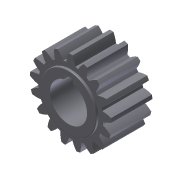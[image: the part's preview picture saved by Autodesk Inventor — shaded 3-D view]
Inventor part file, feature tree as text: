
AUTODESK INVENTOR PART (.ipt)
format: ipt  version: 2011 (Build 150239000, 239)  size: 233,472 bytes
history: native  units: mm (DEFAULTED — no unit token found)
features: other x4, sketch x4, extrude x3, plane x3, fillet x1
ambient origin geometry x8: Origin, YZ Plane, XZ Plane, XY Plane, X Axis, Y Axis, Z Axis, Center Point
bodies: Solid1 (feature_tree)
feature tree (15):
  other  "Gear 17T 20dp 500key"
  extrude  "Extrusion1"  Depth=13.97mm TaperAngle=0.0deg
  plane  "Work Plane1"
  plane  "Work Plane2"
  plane  "Work Plane3"
  other  "Spur Gear"
  extrude  "Extrusion2"  Depth=76.2mm TaperAngle=0.0deg
  extrude  "Extrusion3"  TaperAngle=0.0deg  [1 undecoded]
  fillet  "Fillet1"  Radius=63.5mm
  sketch  "Sketch1"  dims[d0=27.94mm d1=13.97mm d2=0.0mm]
  sketch  "Sketch2"  dims[d3=25.4mm d4=76.2mm d5=0.0mm]
  other  "Srf1"
  sketch  "Sketch3"  dims[d6=0.0mm d7=1.847996mm d9=0.0mm d14=0.0mm d15=63.5mm]
  sketch  "Sketch4"  dims[d16=0.0mm d17=0.0mm d18=0.0mm d19=63.5mm d20=19.05mm d21=0.762mm d22=0.0mm d23=12.7mm d24=3.175mm d25=3.175mm d26=0.762mm d27=0.0mm d28=0.254mm]
  other  "Pitch Diameter"
note: 1 required parameter value undecoded (feature->parameter linkage not recoverable at this tier; creation-order binding heuristic only, values carry confidence <= 0.55)
